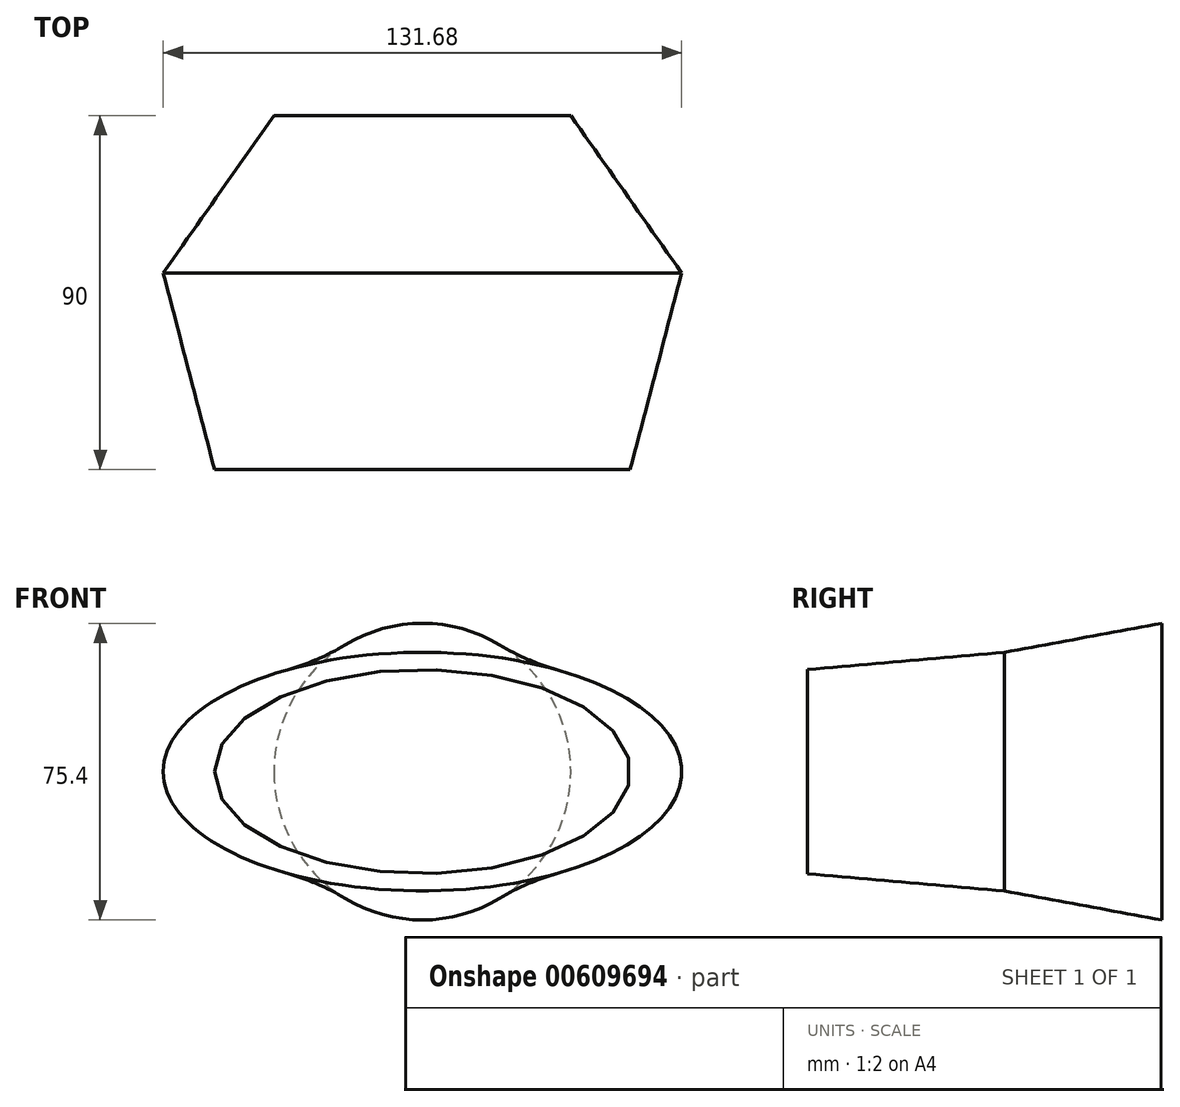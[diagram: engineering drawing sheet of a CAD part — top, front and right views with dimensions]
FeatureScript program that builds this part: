
annotation { "Feature Type Name" : "Feature", "Feature Type Description" : "" }
export const myFeature = defineFeature(function(context is Context, id is Id, definition is map)
    precondition{}
    {
        {
            var Q0;
            Q0=qCreatedBy(makeId("Front.planeOp"),FACE);
            var sketch = newSketch(context, id + "F0", { "sketchPlane" : qUnion([Q0])});
            skEllipse(sketch, "E0", {"center": v(0, 0) * mm, "majorRadius": 65.84 * mm, "minorRadius": 30.3 * mm, "majorAxis": v(-1, 0)});
            skCircle(sketch, "E1", {"center": v(0, 0) * mm, "radius": 18.54 * mm, "construction": true});
            skSolve(sketch);
        }
        {
            var Q0;
            Q0=qCreatedBy(makeId("Front.planeOp"),FACE);
            cPlane(context, id + "F1", {"entities" : qUnion([Q0]), "cplaneType" : CPlaneType.OFFSET, "offset" : 50 * mm, "width" : 150 * mm, "height" : 150 * mm});
        }
        {
            var Q0;
            Q0=qCreatedBy(id+"F1.planeOp",FACE);
            var sketch = newSketch(context, id + "F2", { "sketchPlane" : qUnion([Q0])});
            skEllipse(sketch, "E2", {"center": v(0, 0) * mm, "majorRadius": 52.8 * mm, "minorRadius": 25.95 * mm, "majorAxis": v(-1, 0)});
            skSolve(sketch);
        }
        {
            var Q0;
            Q0=makeQuery(id+"F0.imprint","IMPRINT",FACE,{"disambiguationData":[TD([[makeQuery(id+"F0.imprint","IMPRINT",EDGE,{"derivedFrom":sQuery(id+"F0.wireOp",EDGE,"E0")}),1.0]])]});
            var Q1;
            Q1=makeQuery(id+"F2.imprint","IMPRINT",FACE,{"disambiguationData":[TD([[makeQuery(id+"F2.imprint","IMPRINT",EDGE,{"derivedFrom":sQuery(id+"F2.wireOp",EDGE,"E2")}),1.0]])]});
            loft(context, id + "F3", {"sheetProfilesArray" : [{ "sheetProfileEntities" : qUnion([Q0]) }, { "sheetProfileEntities" : qUnion([Q1]) }]});
        }
        {
            var Q0;
            Q0=qCreatedBy(makeId("Front.planeOp"),FACE);
            cPlane(context, id + "F4", {"entities" : qUnion([Q0]), "cplaneType" : CPlaneType.OFFSET, "offset" : 40 * mm, "oppositeDirection" : true, "width" : 150 * mm, "height" : 150 * mm});
        }
        {
            var Q0;
            Q0=qCreatedBy(id+"F4.planeOp",FACE);
            var sketch = newSketch(context, id + "F5", { "sketchPlane" : qUnion([Q0])});
            skCircle(sketch, "E3", {"center": v(0, 0) * mm, "radius": 37.7 * mm});
            skSolve(sketch);
        }
        {
            var Q1;
            Q1=makeQuery(id+"F3.opLoft","CAP_FACE",FACE,{"disambiguationData":[OSD([makeQuery(id+"F0.imprint","IMPRINT",FACE,{"disambiguationData":[TD([[makeQuery(id+"F0.imprint","IMPRINT",EDGE,{"derivedFrom":sQuery(id+"F0.wireOp",EDGE,"E0")}),1.0]])]})])],"isStart":true});
            var Q2;
            Q2=makeQuery(id+"F5.imprint","IMPRINT",FACE,{"disambiguationData":[TD([[makeQuery(id+"F5.imprint","IMPRINT",EDGE,{"derivedFrom":sQuery(id+"F5.wireOp",EDGE,"E3")}),1.0]])]});
            loft(context, id + "F6", {"operationType" : NewBodyOperationType.ADD, "sheetProfilesArray" : [{ "sheetProfileEntities" : qUnion([Q1]) }, { "sheetProfileEntities" : qUnion([Q2]) }]});
        }
    });
